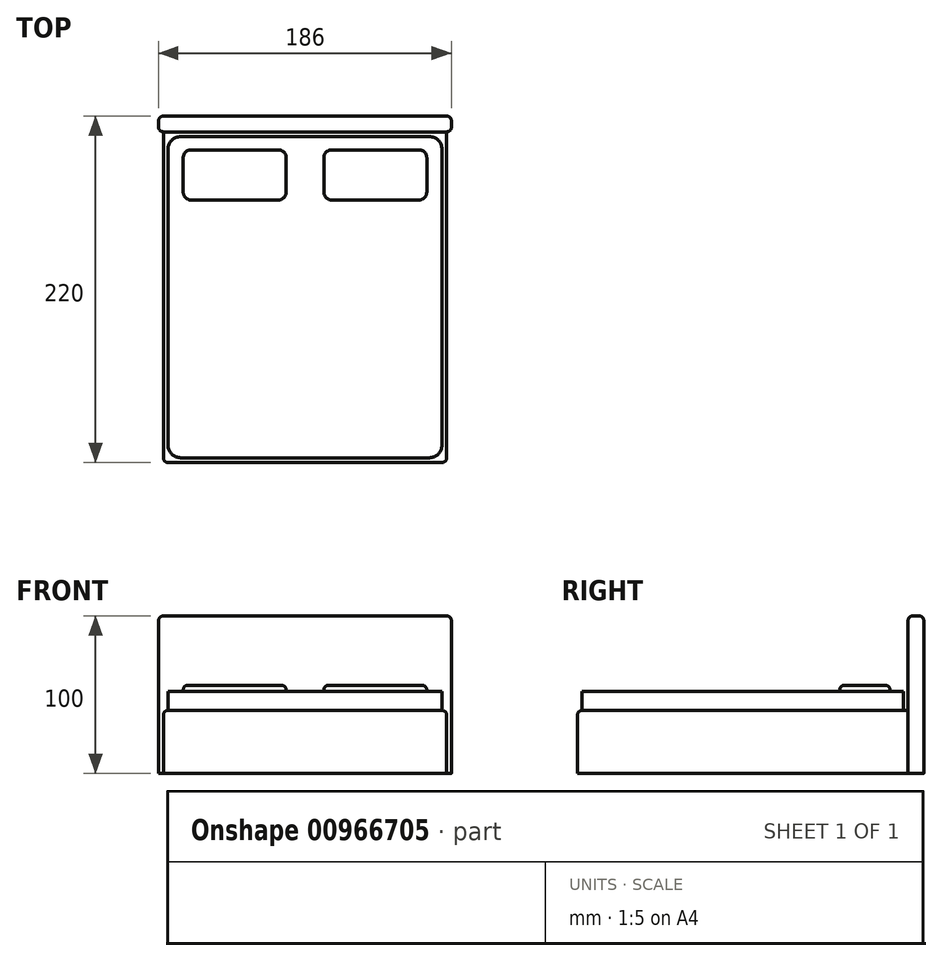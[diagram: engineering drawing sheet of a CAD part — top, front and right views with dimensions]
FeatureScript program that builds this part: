
annotation { "Feature Type Name" : "Feature", "Feature Type Description" : "" }
export const myFeature = defineFeature(function(context is Context, id is Id, definition is map)
    precondition{}
    {
        {
            var Q0;
            Q0=qCreatedBy(makeId("Top.planeOp"),FACE);
            var sketch = newSketch(context, id + "F0", { "sketchPlane" : qUnion([Q0])});
            skLineSegment(sketch, "E0.bottom", {"start": v(-90, 105) * mm, "end": v(90, 105) * mm});
            skLineSegment(sketch, "E0.top", {"start": v(-90, -105) * mm, "end": v(90, -105) * mm});
            skLineSegment(sketch, "E0.left", {"start": v(-90, 105) * mm, "end": v(-90, -105) * mm});
            skLineSegment(sketch, "E0.right", {"start": v(90, 105) * mm, "end": v(90, -105) * mm});
            skLineSegment(sketch, "E1", {"start": v(90, 105) * mm, "end": v(-90, -105) * mm, "construction": true});
            skSolve(sketch);
        }
        {
            var Q0;
            Q0 = qSketchRegion(id + "F0", true);
            extrude(context, id + "F1", {"entities" : qUnion([Q0]), "depth" : 40 * mm, "offsetDistance" : 25 * mm});
        }
        {
            var Q0;
            Q0=qCreatedBy(makeId("Top.planeOp"),FACE);
            var sketch = newSketch(context, id + "F2", { "sketchPlane" : qUnion([Q0])});
            skLineSegment(sketch, "E2.bottom", {"start": v(-93, 115) * mm, "end": v(93, 115) * mm});
            skLineSegment(sketch, "E2.top", {"start": v(-93, 105) * mm, "end": v(93, 105) * mm});
            skLineSegment(sketch, "E2.left", {"start": v(-93, 115) * mm, "end": v(-93, 105) * mm});
            skLineSegment(sketch, "E2.right", {"start": v(93, 115) * mm, "end": v(93, 105) * mm});
            skLineSegment(sketch, "E3", {"start": v(0, 0) * mm, "end": v(0, 105) * mm, "construction": true});
            skSolve(sketch);
        }
        {
            var Q0;
            Q0=makeQuery(id+"F2.imprint","IMPRINT",FACE,{"disambiguationData":[TD([[makeQuery(id+"F2.imprint","IMPRINT",EDGE,{"derivedFrom":sQuery(id+"F2.wireOp",EDGE,"E2.bottom")}),-1.0]])]});
            extrude(context, id + "F3", {"entities" : qUnion([Q0]), "operationType" : NewBodyOperationType.ADD, "depth" : 100 * mm, "offsetDistance" : 25 * mm});
        }
        {
            var Q0;
            Q0=makeQuery(id+"F1.opExtrude","CAP_FACE",FACE,{"disambiguationData":[OSD([sQuery(id+"F0.wireOp",EDGE,"E0.bottom"),sQuery(id+"F0.wireOp",EDGE,"E0.top"),sQuery(id+"F0.wireOp",EDGE,"E0.left"),sQuery(id+"F0.wireOp",EDGE,"E0.right")])],"isStart":false});
            var sketch = newSketch(context, id + "F4", { "sketchPlane" : qUnion([Q0])});
            skLineSegment(sketch, "E4.bottom", {"start": v(-87, 102) * mm, "end": v(87, 102) * mm});
            skLineSegment(sketch, "E4.top", {"start": v(-87, -102) * mm, "end": v(87, -102) * mm});
            skLineSegment(sketch, "E4.left", {"start": v(-87, 102) * mm, "end": v(-87, -102) * mm});
            skLineSegment(sketch, "E4.right", {"start": v(87, 102) * mm, "end": v(87, -102) * mm});
            skSolve(sketch);
        }
        {
            var Q0;
            Q0 = qSketchRegion(id + "F4", true);
            extrude(context, id + "F5", {"entities" : qUnion([Q0]), "operationType" : NewBodyOperationType.ADD, "depth" : 12 * mm, "offsetDistance" : 25 * mm});
        }
        {
            var Q0;
            Q0=makeQuery(id+"F5.opExtrude","CAP_FACE",FACE,{"disambiguationData":[OSD([sQuery(id+"F4.wireOp",EDGE,"E4.bottom"),sQuery(id+"F4.wireOp",EDGE,"E4.top"),sQuery(id+"F4.wireOp",EDGE,"E4.left"),sQuery(id+"F4.wireOp",EDGE,"E4.right")])],"isStart":false});
            var sketch = newSketch(context, id + "F6", { "sketchPlane" : qUnion([Q0])});
            skLineSegment(sketch, "E5.bottom", {"start": v(-77.34, 93.56) * mm, "end": v(-11.98, 93.56) * mm});
            skLineSegment(sketch, "E5.top", {"start": v(-77.34, 61.66) * mm, "end": v(-11.98, 61.66) * mm});
            skLineSegment(sketch, "E5.left", {"start": v(-77.34, 93.56) * mm, "end": v(-77.34, 61.66) * mm});
            skLineSegment(sketch, "E5.right", {"start": v(-11.98, 93.56) * mm, "end": v(-11.98, 61.66) * mm});
            skLineSegment(sketch, "E6", {"start": v(0, 0) * mm, "end": v(0, 102) * mm, "construction": true});
            skLineSegment(sketch, "E7.MirrorCS", {"start": v(77.34, 93.56) * mm, "end": v(11.98, 93.56) * mm});
            skLineSegment(sketch, "E8.MirrorCS", {"start": v(11.98, 93.56) * mm, "end": v(11.98, 61.66) * mm});
            skLineSegment(sketch, "E9.MirrorCS", {"start": v(77.34, 61.66) * mm, "end": v(11.98, 61.66) * mm});
            skLineSegment(sketch, "E10.MirrorCS", {"start": v(77.34, 93.56) * mm, "end": v(77.34, 61.66) * mm});
            skSolve(sketch);
        }
        {
            var Q0;
            Q0=makeQuery(id+"F6.imprint","IMPRINT",FACE,{"disambiguationData":[TD([[makeQuery(id+"F6.imprint","IMPRINT",EDGE,{"derivedFrom":sQuery(id+"F6.wireOp",EDGE,"E5.bottom")}),-1.0]])]});
            extrude(context, id + "F7", {"entities" : qUnion([Q0]), "operationType" : NewBodyOperationType.ADD, "depth" : 4 * mm, "offsetDistance" : 25 * mm});
        }
        {
            var Q0;
            Q0 = qSketchRegion(id + "F6", true);
            extrude(context, id + "F8", {"entities" : qUnion([Q0]), "operationType" : NewBodyOperationType.ADD, "depth" : 4 * mm, "offsetDistance" : 25 * mm});
        }
        {
            var Q0;
            Q0=makeQuery(id+"F5.opExtrude","SWEPT_EDGE",EDGE,{"disambiguationData":[OSD([sQuery(id+"F4.wireOp",EDGE,"E4.top"),sQuery(id+"F4.wireOp",EDGE,"E4.left")])]});
            var Q1;
            Q1=makeQuery(id+"F5.opExtrude","SWEPT_EDGE",EDGE,{"disambiguationData":[OSD([sQuery(id+"F4.wireOp",EDGE,"E4.top"),sQuery(id+"F4.wireOp",EDGE,"E4.right")])]});
            var Q2;
            Q2=makeQuery(id+"F5.opExtrude","SWEPT_EDGE",EDGE,{"disambiguationData":[OSD([sQuery(id+"F4.wireOp",EDGE,"E4.bottom"),sQuery(id+"F4.wireOp",EDGE,"E4.right")])]});
            var Q3;
            Q3=makeQuery(id+"F5.opExtrude","SWEPT_EDGE",EDGE,{"disambiguationData":[OSD([sQuery(id+"F4.wireOp",EDGE,"E4.bottom"),sQuery(id+"F4.wireOp",EDGE,"E4.left")])]});
            fillet(context, id + "F9", {"entities" : qUnion([Q0, Q1, Q2, Q3]), "radius" : 8 * mm, "tangentPropagation" : true, "allowEdgeOverflow" : false});
        }
        {
            var Q0;
            Q0=makeQuery(id+"F3.opExtrude","CAP_EDGE",EDGE,{"disambiguationData":[OSD([sQuery(id+"F2.wireOp",EDGE,"E2.left")])],"isStart":false});
            var Q1;
            Q1=makeQuery(id+"F3.opExtrude","SWEPT_EDGE",EDGE,{"disambiguationData":[OSD([sQuery(id+"F2.wireOp",EDGE,"E2.top"),sQuery(id+"F2.wireOp",EDGE,"E2.left")])]});
            var Q2;
            Q2=makeQuery(id+"F3.opExtrude","CAP_EDGE",EDGE,{"disambiguationData":[OSD([sQuery(id+"F2.wireOp",EDGE,"E2.top")])],"isStart":false});
            var Q3;
            Q3=makeQuery(id+"F3.opExtrude","SWEPT_EDGE",EDGE,{"disambiguationData":[OSD([sQuery(id+"F2.wireOp",EDGE,"E2.top"),sQuery(id+"F2.wireOp",EDGE,"E2.right")])]});
            var Q4;
            Q4=makeQuery(id+"F3.opExtrude","CAP_EDGE",EDGE,{"disambiguationData":[OSD([sQuery(id+"F2.wireOp",EDGE,"E2.right")])],"isStart":false});
            var Q5;
            Q5=makeQuery(id+"F3.opExtrude","CAP_EDGE",EDGE,{"disambiguationData":[OSD([sQuery(id+"F2.wireOp",EDGE,"E2.bottom")])],"isStart":false});
            var Q6;
            Q6=makeQuery(id+"F3.opExtrude","SWEPT_EDGE",EDGE,{"disambiguationData":[OSD([sQuery(id+"F2.wireOp",EDGE,"E2.bottom"),sQuery(id+"F2.wireOp",EDGE,"E2.left")])]});
            var Q7;
            Q7=makeQuery(id+"F3.opExtrude","SWEPT_EDGE",EDGE,{"disambiguationData":[OSD([sQuery(id+"F2.wireOp",EDGE,"E2.bottom"),sQuery(id+"F2.wireOp",EDGE,"E2.right")])]});
            fillet(context, id + "F10", {"entities" : qUnion([Q0, Q1, Q2, Q3, Q4, Q5, Q6, Q7]), "radius" : 3 * mm, "tangentPropagation" : true, "allowEdgeOverflow" : false});
        }
        {
            var Q0;
            Q0=makeQuery(id+"F1.opExtrude","CAP_EDGE",EDGE,{"disambiguationData":[OSD([sQuery(id+"F0.wireOp",EDGE,"E0.left")])],"isStart":false});
            var Q1;
            Q1=makeQuery(id+"F1.opExtrude","CAP_EDGE",EDGE,{"disambiguationData":[OSD([sQuery(id+"F0.wireOp",EDGE,"E0.top")])],"isStart":false});
            var Q2;
            Q2=makeQuery(id+"F1.opExtrude","SWEPT_EDGE",EDGE,{"disambiguationData":[OSD([sQuery(id+"F0.wireOp",EDGE,"E0.top"),sQuery(id+"F0.wireOp",EDGE,"E0.left")])]});
            var Q3;
            Q3=makeQuery(id+"F1.opExtrude","SWEPT_EDGE",EDGE,{"disambiguationData":[OSD([sQuery(id+"F0.wireOp",EDGE,"E0.top"),sQuery(id+"F0.wireOp",EDGE,"E0.right")])]});
            var Q4;
            Q4=makeQuery(id+"F1.opExtrude","CAP_EDGE",EDGE,{"disambiguationData":[OSD([sQuery(id+"F0.wireOp",EDGE,"E0.right")])],"isStart":false});
            fillet(context, id + "F11", {"entities" : qUnion([Q0, Q1, Q2, Q3, Q4]), "radius" : 3 * mm, "tangentPropagation" : true, "allowEdgeOverflow" : false});
        }
        {
            var Q0;
            Q0=makeQuery(id+"F7.opExtrude","SWEPT_EDGE",EDGE,{"disambiguationData":[OSD([sQuery(id+"F6.wireOp",EDGE,"E5.top"),sQuery(id+"F6.wireOp",EDGE,"E5.left")])]});
            var Q1;
            Q1=makeQuery(id+"F7.opExtrude","SWEPT_EDGE",EDGE,{"disambiguationData":[OSD([sQuery(id+"F6.wireOp",EDGE,"E5.top"),sQuery(id+"F6.wireOp",EDGE,"E5.right")])]});
            var Q2;
            Q2=makeQuery(id+"F7.opExtrude","SWEPT_EDGE",EDGE,{"disambiguationData":[OSD([sQuery(id+"F6.wireOp",EDGE,"E5.bottom"),sQuery(id+"F6.wireOp",EDGE,"E5.right")])]});
            var Q3;
            Q3=makeQuery(id+"F7.opExtrude","SWEPT_EDGE",EDGE,{"disambiguationData":[OSD([sQuery(id+"F6.wireOp",EDGE,"E5.bottom"),sQuery(id+"F6.wireOp",EDGE,"E5.left")])]});
            var Q4;
            Q4=makeQuery(id+"F8.opExtrude","SWEPT_EDGE",EDGE,{"disambiguationData":[OSD([sQuery(id+"F6.wireOp",EDGE,"E7.MirrorCS"),sQuery(id+"F6.wireOp",EDGE,"E8.MirrorCS")])]});
            var Q5;
            Q5=makeQuery(id+"F8.opExtrude","SWEPT_EDGE",EDGE,{"disambiguationData":[OSD([sQuery(id+"F6.wireOp",EDGE,"E8.MirrorCS"),sQuery(id+"F6.wireOp",EDGE,"E9.MirrorCS")])]});
            var Q6;
            Q6=makeQuery(id+"F8.opExtrude","SWEPT_EDGE",EDGE,{"disambiguationData":[OSD([sQuery(id+"F6.wireOp",EDGE,"E9.MirrorCS"),sQuery(id+"F6.wireOp",EDGE,"E10.MirrorCS")])]});
            var Q7;
            Q7=makeQuery(id+"F8.opExtrude","SWEPT_EDGE",EDGE,{"disambiguationData":[OSD([sQuery(id+"F6.wireOp",EDGE,"E7.MirrorCS"),sQuery(id+"F6.wireOp",EDGE,"E10.MirrorCS")])]});
            fillet(context, id + "F12", {"entities" : qUnion([Q0, Q1, Q2, Q3, Q4, Q5, Q6, Q7]), "radius" : 5 * mm, "tangentPropagation" : true, "allowEdgeOverflow" : false});
        }
        {
            var Q0;
            Q0=makeQuery(id+"F8.opExtrude","CAP_FACE",FACE,{"disambiguationData":[OSD([sQuery(id+"F6.wireOp",EDGE,"E7.MirrorCS"),sQuery(id+"F6.wireOp",EDGE,"E8.MirrorCS"),sQuery(id+"F6.wireOp",EDGE,"E9.MirrorCS"),sQuery(id+"F6.wireOp",EDGE,"E10.MirrorCS")])],"isStart":false});
            var Q1;
            Q1=makeQuery(id+"F7.opExtrude","CAP_FACE",FACE,{"disambiguationData":[OSD([sQuery(id+"F6.wireOp",EDGE,"E5.bottom"),sQuery(id+"F6.wireOp",EDGE,"E5.top"),sQuery(id+"F6.wireOp",EDGE,"E5.left"),sQuery(id+"F6.wireOp",EDGE,"E5.right")])],"isStart":false});
            fillet(context, id + "F13", {"entities" : qUnion([Q0, Q1]), "radius" : 3 * mm, "tangentPropagation" : true, "allowEdgeOverflow" : false});
        }
    });
